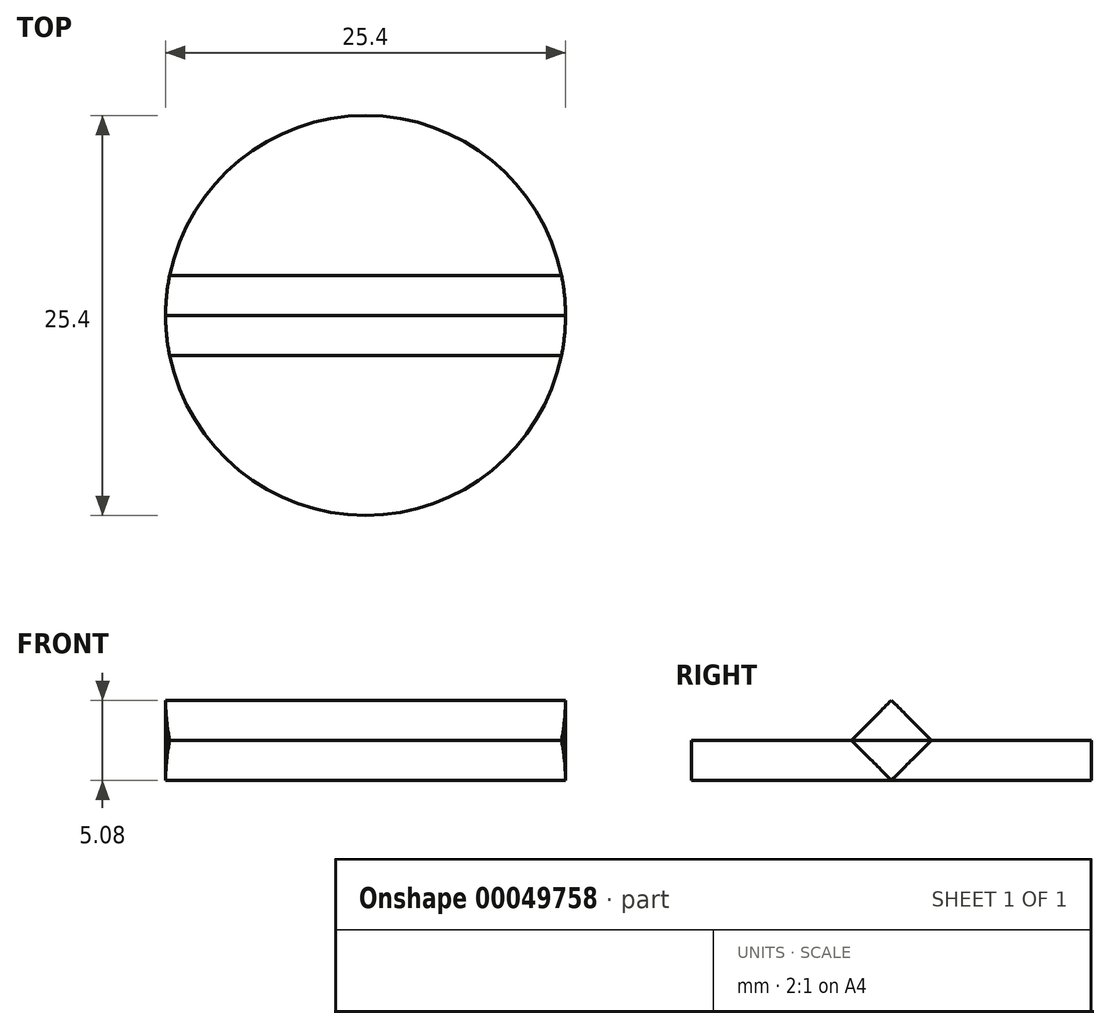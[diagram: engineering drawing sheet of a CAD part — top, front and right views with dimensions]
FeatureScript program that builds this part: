
annotation { "Feature Type Name" : "Feature", "Feature Type Description" : "" }
export const myFeature = defineFeature(function(context is Context, id is Id, definition is map)
    precondition{}
    {
        {
            var Q0;
            Q0=qCreatedBy(makeId("Top.planeOp"),FACE);
            var sketch = newSketch(context, id + "F0", { "sketchPlane" : qUnion([Q0])});
            skCircle(sketch, "E0", {"center": v(0, 0) * mm, "radius": 12.7 * mm});
            skSolve(sketch);
        }
        {
            var Q0;
            Q0=qCreatedBy(makeId("Top.planeOp"),FACE);
            var sketch = newSketch(context, id + "F1", { "sketchPlane" : qUnion([Q0])});
            skCircle(sketch, "E1", {"center": v(0, 0) * mm, "radius": 1.27 * mm});
            skSolve(sketch);
        }
        {
            var Q0;
            Q0=qCreatedBy(makeId("Right.planeOp"),FACE);
            var sketch = newSketch(context, id + "F2", { "sketchPlane" : qUnion([Q0])});
            skCircle(sketch, "E2.cCircle", {"center": v(0, 0) * mm, "radius": 2.54 * mm, "construction": true});
            skLineSegment(sketch, "E2.0", {"start": v(2.54, 0) * mm, "end": v(0, -2.54) * mm});
            skLineSegment(sketch, "E2.1", {"start": v(0, -2.54) * mm, "end": v(-2.54, 0) * mm});
            skLineSegment(sketch, "E2.2", {"start": v(-2.54, 0) * mm, "end": v(0, 2.54) * mm});
            skLineSegment(sketch, "E2.3", {"start": v(0, 2.54) * mm, "end": v(2.54, 0) * mm});
            skSolve(sketch);
        }
        {
            var Q0;
            Q0=qSketchRegion(id+"F2",true);
            extrude(context, id + "F3", {"entities" : qUnion([Q0]), "endBound" : BoundingType.SYMMETRIC, "oppositeDirection" : true, "depth" : 25.4 * mm});
        }
        {
            var Q0;
            Q0=qSketchRegion(id+"F0",true);
            extrude(context, id + "F4", {"entities" : qUnion([Q0]), "oppositeDirection" : true, "depth" : 2.54 * mm});
        }
        {
            var Q0;
            Q0=makeQuery(id+"F0.imprint","IMPRINT",FACE,{"disambiguationData":[TD([[makeQuery(id+"F0.imprint","IMPRINT",EDGE,{"derivedFrom":sQuery(id+"F0.wireOp",EDGE,"E0")}),1.0]])]});
            var sketch = newSketch(context, id + "F5", { "sketchPlane" : qUnion([Q0])});
            skCircle(sketch, "E3", {"center": v(0, 0) * mm, "radius": 15.24 * mm});
            skCircle(sketch, "E4", {"center": v(0, 0) * mm, "radius": 12.7 * mm});
            skSolve(sketch);
        }
        {
            var Q0;
            Q0=qSketchRegion(id+"F5",true);
            extrude(context, id + "F6", {"entities" : qUnion([Q0]), "operationType" : NewBodyOperationType.REMOVE, "endBound" : BoundingType.SYMMETRIC, "depth" : 12.7 * mm});
        }
    });
